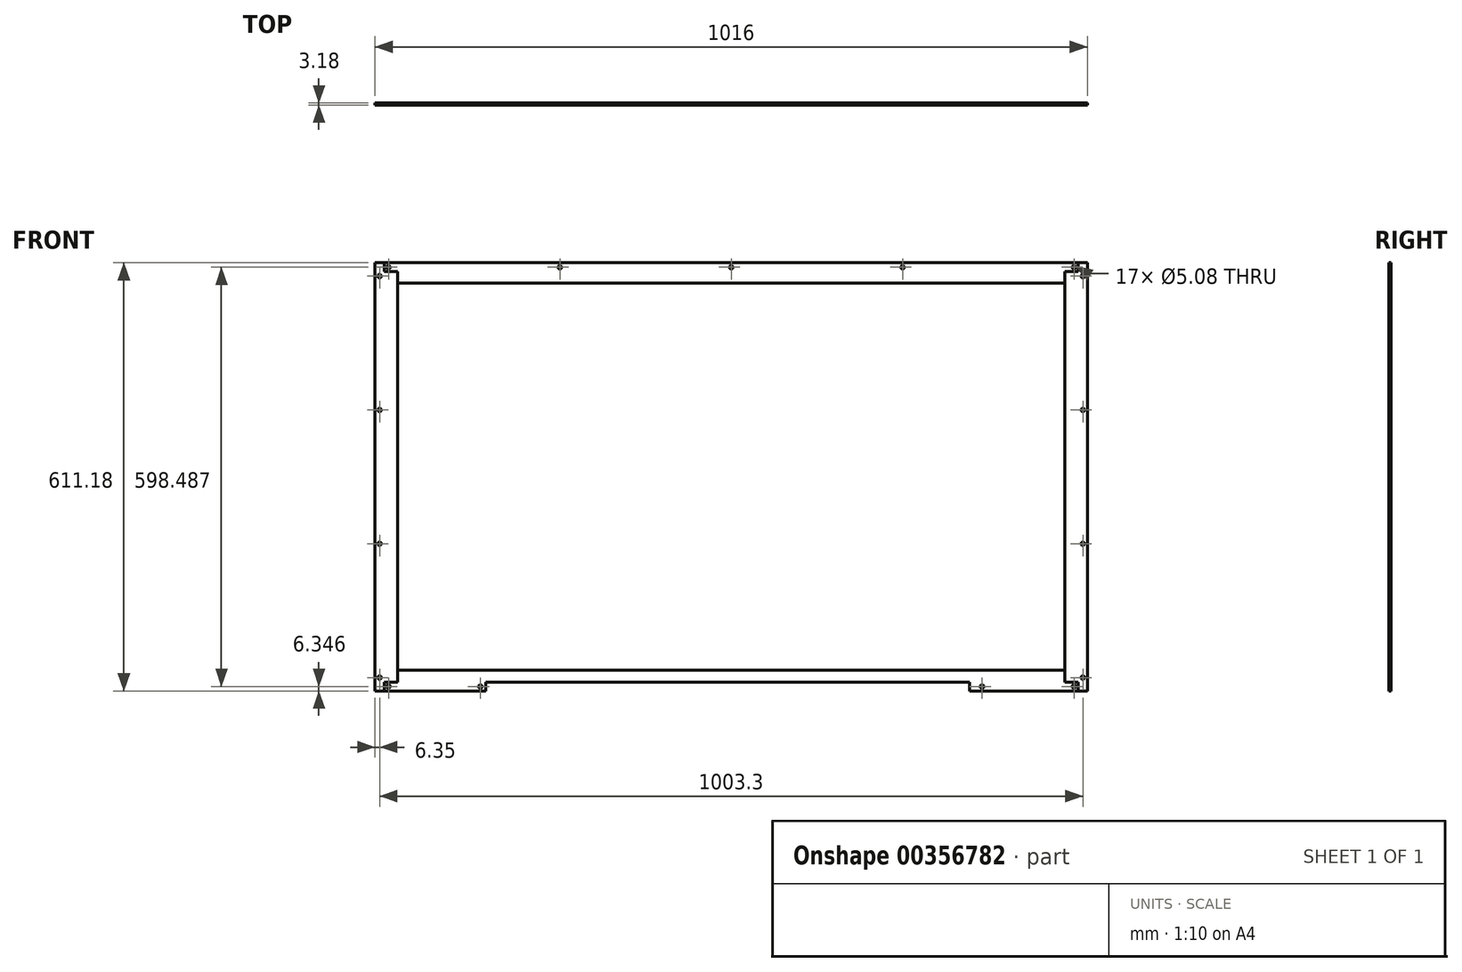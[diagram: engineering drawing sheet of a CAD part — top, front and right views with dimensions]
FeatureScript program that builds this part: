
annotation { "Feature Type Name" : "Feature", "Feature Type Description" : "" }
export const myFeature = defineFeature(function(context is Context, id is Id, definition is map)
    precondition{}
    {
        {
            var Q0;
            Q0=qCreatedBy(makeId("Front.planeOp"),FACE);
            var sketch = newSketch(context, id + "F0", { "sketchPlane" : qUnion([Q0])});
            skLineSegment(sketch, "E0.bottom", {"start": v(495.3, 292.9) * mm, "end": v(-495.3, 292.9) * mm});
            skLineSegment(sketch, "E0.top", {"start": v(495.3, -292.9) * mm, "end": v(-495.3, -292.9) * mm});
            skLineSegment(sketch, "E0.left", {"start": v(495.3, 292.9) * mm, "end": v(495.3, -292.9) * mm});
            skLineSegment(sketch, "E0.right", {"start": v(-495.3, 292.9) * mm, "end": v(-495.3, -292.9) * mm});
            skPoint(sketch, "E0.middle", {"position": v(0, 0) * mm});
            skLineSegment(sketch, "E1.0", {"start": v(-508, 305.6) * mm, "end": v(-508, -305.6) * mm});
            skLineSegment(sketch, "E1.1", {"start": v(508, 305.6) * mm, "end": v(-508, 305.6) * mm});
            skLineSegment(sketch, "E1.2", {"start": v(508, 305.6) * mm, "end": v(508, -305.6) * mm});
            skLineSegment(sketch, "E1.3", {"start": v(508, -305.6) * mm, "end": v(-508, -305.6) * mm});
            skLineSegment(sketch, "E2", {"start": v(-508, 305.6) * mm, "end": v(-495.3, 292.9) * mm});
            skPoint(sketch, "E3.middle", {"position": v(-501.65, 299.24) * mm});
            skLineSegment(sketch, "E4.bottom", {"start": v(-355.3, -296.7) * mm, "end": v(-360.38, -296.7) * mm});
            skLineSegment(sketch, "E4.top", {"start": v(-355.3, -301.78) * mm, "end": v(-360.38, -301.78) * mm});
            skLineSegment(sketch, "E4.left", {"start": v(-355.3, -296.7) * mm, "end": v(-355.3, -301.78) * mm});
            skLineSegment(sketch, "E4.right", {"start": v(-360.38, -296.7) * mm, "end": v(-360.38, -301.78) * mm});
            skPoint(sketch, "E4.middle", {"position": v(-357.84, -299.24) * mm});
            skLineSegment(sketch, "E5.MirrorCS", {"start": v(360.38, -296.7) * mm, "end": v(360.38, -301.78) * mm});
            skLineSegment(sketch, "E6.MirrorCS", {"start": v(355.3, -296.7) * mm, "end": v(360.38, -296.7) * mm});
            skLineSegment(sketch, "E7.MirrorCS", {"start": v(355.3, -296.7) * mm, "end": v(355.3, -301.78) * mm});
            skLineSegment(sketch, "E8.MirrorCS", {"start": v(355.3, -301.78) * mm, "end": v(360.38, -301.78) * mm});
            skLineSegment(sketch, "E9.bottom", {"start": v(-486.41, 296.7) * mm, "end": v(-491.5, 296.7) * mm});
            skLineSegment(sketch, "E9.top", {"start": v(-486.41, 301.78) * mm, "end": v(-491.5, 301.78) * mm});
            skLineSegment(sketch, "E9.left", {"start": v(-486.41, 296.7) * mm, "end": v(-486.41, 301.78) * mm});
            skLineSegment(sketch, "E9.right", {"start": v(-491.5, 296.7) * mm, "end": v(-491.5, 301.78) * mm});
            skPoint(sketch, "E9.middle", {"position": v(-488.95, 299.24) * mm});
            skLineSegment(sketch, "E10.MirrorCS", {"start": v(-504.2, 284) * mm, "end": v(-504.2, 289.08) * mm});
            skLineSegment(sketch, "E11.MirrorCS", {"start": v(-499.11, 289.08) * mm, "end": v(-504.2, 289.08) * mm});
            skLineSegment(sketch, "E12.MirrorCS", {"start": v(-499.11, 284) * mm, "end": v(-499.11, 289.08) * mm});
            skLineSegment(sketch, "E13.MirrorCS", {"start": v(-499.11, 284) * mm, "end": v(-504.2, 284) * mm});
            skCircle(sketch, "E14", {"center": v(-488.95, 299.24) * mm, "radius": 5.97 * mm});
            skLineSegment(sketch, "E15.MirrorCS", {"start": v(499.11, 284) * mm, "end": v(499.11, 289.08) * mm});
            skLineSegment(sketch, "E16.MirrorCS", {"start": v(499.11, 284) * mm, "end": v(504.2, 284) * mm});
            skLineSegment(sketch, "E17.MirrorCS", {"start": v(499.11, 289.08) * mm, "end": v(504.2, 289.08) * mm});
            skLineSegment(sketch, "E18.MirrorCS", {"start": v(504.2, 284) * mm, "end": v(504.2, 289.08) * mm});
            skLineSegment(sketch, "E19.MirrorCS", {"start": v(486.41, 301.78) * mm, "end": v(491.5, 301.78) * mm});
            skLineSegment(sketch, "E20.MirrorCS", {"start": v(486.41, 296.7) * mm, "end": v(486.41, 301.78) * mm});
            skLineSegment(sketch, "E21.MirrorCS", {"start": v(486.41, 296.7) * mm, "end": v(491.5, 296.7) * mm});
            skLineSegment(sketch, "E22.MirrorCS", {"start": v(491.5, 296.7) * mm, "end": v(491.5, 301.78) * mm});
            skPoint(sketch, "E23.MirrorP", {"position": v(488.95, 299.24) * mm});
            skLineSegment(sketch, "E24.MirrorCS", {"start": v(-499.11, -289.08) * mm, "end": v(-504.2, -289.08) * mm});
            skLineSegment(sketch, "E25.MirrorCS", {"start": v(-499.11, -284) * mm, "end": v(-499.11, -289.08) * mm});
            skLineSegment(sketch, "E26.MirrorCS", {"start": v(-499.11, -284) * mm, "end": v(-504.2, -284) * mm});
            skLineSegment(sketch, "E27.MirrorCS", {"start": v(-504.2, -284) * mm, "end": v(-504.2, -289.08) * mm});
            skLineSegment(sketch, "E28.MirrorCS", {"start": v(-486.41, -301.78) * mm, "end": v(-491.5, -301.78) * mm});
            skLineSegment(sketch, "E29.MirrorCS", {"start": v(-491.5, -296.7) * mm, "end": v(-491.5, -301.78) * mm});
            skPoint(sketch, "E30.MirrorP", {"position": v(-488.95, -299.24) * mm});
            skLineSegment(sketch, "E31.MirrorCS", {"start": v(-486.41, -296.7) * mm, "end": v(-486.41, -301.78) * mm});
            skLineSegment(sketch, "E32.MirrorCS", {"start": v(-486.41, -296.7) * mm, "end": v(-491.5, -296.7) * mm});
            skLineSegment(sketch, "E33.MirrorCS", {"start": v(486.41, -296.7) * mm, "end": v(486.41, -301.78) * mm});
            skPoint(sketch, "E34.MirrorP", {"position": v(488.95, -299.24) * mm});
            skLineSegment(sketch, "E35.MirrorCS", {"start": v(491.5, -296.7) * mm, "end": v(491.5, -301.78) * mm});
            skLineSegment(sketch, "E36.MirrorCS", {"start": v(486.41, -296.7) * mm, "end": v(491.5, -296.7) * mm});
            skLineSegment(sketch, "E37.MirrorCS", {"start": v(486.41, -301.78) * mm, "end": v(491.5, -301.78) * mm});
            skLineSegment(sketch, "E38.MirrorCS", {"start": v(499.11, -289.08) * mm, "end": v(504.2, -289.08) * mm});
            skLineSegment(sketch, "E39.MirrorCS", {"start": v(504.2, -284) * mm, "end": v(504.2, -289.08) * mm});
            skLineSegment(sketch, "E40.MirrorCS", {"start": v(499.11, -284) * mm, "end": v(499.11, -289.08) * mm});
            skLineSegment(sketch, "E41.MirrorCS", {"start": v(499.11, -284) * mm, "end": v(504.2, -284) * mm});
            skLineSegment(sketch, "E42.bottom", {"start": v(-504.19, 92.97) * mm, "end": v(-499.11, 92.97) * mm});
            skLineSegment(sketch, "E42.top", {"start": v(-504.19, 98.05) * mm, "end": v(-499.11, 98.05) * mm});
            skLineSegment(sketch, "E42.left", {"start": v(-504.2, 92.97) * mm, "end": v(-504.2, 98.05) * mm});
            skLineSegment(sketch, "E42.right", {"start": v(-499.11, 92.97) * mm, "end": v(-499.11, 98.05) * mm});
            skPoint(sketch, "E42.middle", {"position": v(-501.65, 95.51) * mm});
            skLineSegment(sketch, "E43.bottom", {"start": v(-499.11, -92.97) * mm, "end": v(-504.19, -92.97) * mm});
            skLineSegment(sketch, "E43.top", {"start": v(-499.11, -98.05) * mm, "end": v(-504.19, -98.05) * mm});
            skLineSegment(sketch, "E43.left", {"start": v(-499.11, -92.97) * mm, "end": v(-499.11, -98.05) * mm});
            skLineSegment(sketch, "E43.right", {"start": v(-504.2, -92.97) * mm, "end": v(-504.2, -98.05) * mm});
            skPoint(sketch, "E43.middle", {"position": v(-501.65, -95.51) * mm});
            skLineSegment(sketch, "E44", {"start": v(-501.65, -284) * mm, "end": v(-501.65, -98.05) * mm});
            skLineSegment(sketch, "E45", {"start": v(-501.65, -92.97) * mm, "end": v(-501.65, 92.97) * mm});
            skLineSegment(sketch, "E46", {"start": v(-501.65, 98.05) * mm, "end": v(-501.65, 284) * mm});
            skLineSegment(sketch, "E47.bottom", {"start": v(2.54, 301.78) * mm, "end": v(-2.54, 301.78) * mm});
            skLineSegment(sketch, "E47.top", {"start": v(2.54, 296.7) * mm, "end": v(-2.54, 296.7) * mm});
            skLineSegment(sketch, "E47.left", {"start": v(2.54, 301.78) * mm, "end": v(2.54, 296.7) * mm});
            skLineSegment(sketch, "E47.right", {"start": v(-2.54, 301.78) * mm, "end": v(-2.54, 296.7) * mm});
            skPoint(sketch, "E47.middle", {"position": v(0, 299.24) * mm});
            skPoint(sketch, "E47.middle.positionSnap0", {"position": v(0, 305.6) * mm});
            skPoint(sketch, "E47.centerSnap0", {"position": v(0, 305.6) * mm});
            skLineSegment(sketch, "E48.bottom", {"start": v(-241.94, 301.78) * mm, "end": v(-247.02, 301.78) * mm});
            skLineSegment(sketch, "E48.top", {"start": v(-241.94, 296.7) * mm, "end": v(-247.02, 296.7) * mm});
            skLineSegment(sketch, "E48.left", {"start": v(-241.94, 301.78) * mm, "end": v(-241.94, 296.7) * mm});
            skLineSegment(sketch, "E48.right", {"start": v(-247.02, 301.78) * mm, "end": v(-247.02, 296.7) * mm});
            skPoint(sketch, "E48.middle", {"position": v(-244.48, 299.24) * mm});
            skLineSegment(sketch, "E49.MirrorCS", {"start": v(241.94, 296.7) * mm, "end": v(247.02, 296.7) * mm});
            skPoint(sketch, "E50.MirrorP", {"position": v(244.48, 299.24) * mm});
            skLineSegment(sketch, "E51.MirrorCS", {"start": v(247.02, 301.78) * mm, "end": v(247.02, 296.7) * mm});
            skLineSegment(sketch, "E52.MirrorCS", {"start": v(241.94, 301.78) * mm, "end": v(247.02, 301.78) * mm});
            skLineSegment(sketch, "E53.MirrorCS", {"start": v(241.94, 301.78) * mm, "end": v(241.94, 296.7) * mm});
            skLineSegment(sketch, "E54.MirrorCS", {"start": v(504.19, 92.97) * mm, "end": v(499.11, 92.97) * mm});
            skLineSegment(sketch, "E55.MirrorCS", {"start": v(499.11, 92.97) * mm, "end": v(499.11, 98.05) * mm});
            skPoint(sketch, "E56.MirrorP", {"position": v(501.65, 95.51) * mm});
            skLineSegment(sketch, "E57.MirrorCS", {"start": v(504.19, 98.05) * mm, "end": v(499.11, 98.05) * mm});
            skLineSegment(sketch, "E58.MirrorCS", {"start": v(504.2, 92.97) * mm, "end": v(504.2, 98.05) * mm});
            skLineSegment(sketch, "E59.MirrorCS", {"start": v(499.11, -98.05) * mm, "end": v(504.19, -98.05) * mm});
            skLineSegment(sketch, "E60.MirrorCS", {"start": v(499.11, -92.97) * mm, "end": v(499.11, -98.05) * mm});
            skLineSegment(sketch, "E61.MirrorCS", {"start": v(499.11, -92.97) * mm, "end": v(504.19, -92.97) * mm});
            skPoint(sketch, "E62.MirrorP", {"position": v(501.65, -95.51) * mm});
            skLineSegment(sketch, "E63.MirrorCS", {"start": v(504.2, -92.97) * mm, "end": v(504.2, -98.05) * mm});
            skCircle(sketch, "E64", {"center": v(-488.95, 299.24) * mm, "radius": 2.54 * mm});
            skCircle(sketch, "E65", {"center": v(-501.65, 286.54) * mm, "radius": 2.54 * mm});
            skPoint(sketch, "E65.centerSnap0", {"position": v(-499.11, 286.54) * mm});
            skPoint(sketch, "E65.centerSnap1", {"position": v(-501.65, 289.08) * mm});
            skCircle(sketch, "E66", {"center": v(-501.65, 95.51) * mm, "radius": 2.54 * mm});
            skCircle(sketch, "E67", {"center": v(-501.65, -95.51) * mm, "radius": 2.54 * mm});
            skCircle(sketch, "E68", {"center": v(-501.65, -286.54) * mm, "radius": 2.54 * mm});
            skPoint(sketch, "E68.centerSnap0", {"position": v(-499.11, -286.54) * mm});
            skPoint(sketch, "E68.centerSnap1", {"position": v(-501.65, -289.08) * mm});
            skCircle(sketch, "E69", {"center": v(-488.95, -299.24) * mm, "radius": 2.54 * mm});
            skCircle(sketch, "E70", {"center": v(-357.84, -299.24) * mm, "radius": 2.54 * mm});
            skCircle(sketch, "E71", {"center": v(357.84, -299.24) * mm, "radius": 2.54 * mm});
            skPoint(sketch, "E71.centerSnap0", {"position": v(357.84, -296.7) * mm});
            skCircle(sketch, "E72", {"center": v(488.95, -299.24) * mm, "radius": 2.54 * mm});
            skCircle(sketch, "E73", {"center": v(501.65, -286.54) * mm, "radius": 2.54 * mm});
            skPoint(sketch, "E73.centerSnap0", {"position": v(501.65, -289.08) * mm});
            skPoint(sketch, "E73.centerSnap1", {"position": v(499.11, -286.54) * mm});
            skCircle(sketch, "E74", {"center": v(501.65, -95.51) * mm, "radius": 2.54 * mm});
            skCircle(sketch, "E75", {"center": v(501.65, 95.51) * mm, "radius": 2.54 * mm});
            skCircle(sketch, "E76", {"center": v(501.65, 286.54) * mm, "radius": 2.54 * mm});
            skPoint(sketch, "E76.centerSnap0", {"position": v(504.19, 286.54) * mm});
            skPoint(sketch, "E76.centerSnap1", {"position": v(501.65, 289.08) * mm});
            skCircle(sketch, "E77", {"center": v(488.95, 299.24) * mm, "radius": 2.54 * mm});
            skCircle(sketch, "E78", {"center": v(244.48, 299.24) * mm, "radius": 2.54 * mm});
            skCircle(sketch, "E79", {"center": v(0, 299.24) * mm, "radius": 2.54 * mm});
            skCircle(sketch, "E80", {"center": v(-244.48, 299.24) * mm, "radius": 2.54 * mm});
            skLineSegment(sketch, "E81", {"start": v(-495.3, 292.9) * mm, "end": v(-508, 292.9) * mm});
            skLineSegment(sketch, "E82", {"start": v(495.3, 292.9) * mm, "end": v(508, 292.9) * mm});
            skLineSegment(sketch, "E83", {"start": v(-495.3, -292.9) * mm, "end": v(-508, -292.9) * mm});
            skLineSegment(sketch, "E84", {"start": v(495.3, -292.9) * mm, "end": v(508, -292.9) * mm});
            skLineSegment(sketch, "E85", {"start": v(-350.3, -292.9) * mm, "end": v(-350.3, -305.6) * mm});
            skLineSegment(sketch, "E86", {"start": v(340.3, -292.9) * mm, "end": v(340.3, -305.6) * mm});
            skLineSegment(sketch, "E87.bottom", {"start": v(476, 276.23) * mm, "end": v(-476, 276.23) * mm});
            skLineSegment(sketch, "E87.top", {"start": v(476, -276.22) * mm, "end": v(-476, -276.23) * mm});
            skLineSegment(sketch, "E87.left", {"start": v(476, 276.23) * mm, "end": v(476, -276.23) * mm});
            skLineSegment(sketch, "E87.right", {"start": v(-476, 276.23) * mm, "end": v(-476, -276.23) * mm});
            skLineSegment(sketch, "E88", {"start": v(-476, 276.23) * mm, "end": v(-476, 292.9) * mm});
            skLineSegment(sketch, "E89", {"start": v(-495.3, 292.9) * mm, "end": v(-495.3, 305.6) * mm});
            skLineSegment(sketch, "E90", {"start": v(-476, -276.23) * mm, "end": v(-476, -292.9) * mm});
            skLineSegment(sketch, "E91", {"start": v(-495.3, -292.9) * mm, "end": v(-495.3, -305.6) * mm});
            skLineSegment(sketch, "E92", {"start": v(476, 276.23) * mm, "end": v(476, 292.9) * mm});
            skLineSegment(sketch, "E93", {"start": v(495.3, 292.9) * mm, "end": v(495.3, 305.6) * mm});
            skLineSegment(sketch, "E94", {"start": v(-350.3, -292.9) * mm, "end": v(-350.3, -276.23) * mm});
            skLineSegment(sketch, "E95", {"start": v(476, -276.22) * mm, "end": v(476, -292.9) * mm});
            skLineSegment(sketch, "E96", {"start": v(340.3, -292.9) * mm, "end": v(340.3, -276.22) * mm});
            skLineSegment(sketch, "E97", {"start": v(495.3, -292.9) * mm, "end": v(495.3, -305.6) * mm});
            skSolve(sketch);
        }
        {
            var Q0;
            {var subQ3=sQuery(id+"F0.wireOp",EDGE,"E83");Q0=makeQuery(id+"F0.imprint","IMPRINT",FACE,{"disambiguationData":[TD([[makeQuery(id+"F0.imprint","IMPRINT",EDGE,{"derivedFrom":subQ3}),1.0]])]});}
            var Q1;
            {var subQ0=sQuery(id+"F0.wireOp",EDGE,"E0.right");Q1=makeQuery(id+"F0.imprint","IMPRINT",FACE,{"disambiguationData":[TD([[makeQuery(id+"F0.imprint","IMPRINT",EDGE,{"derivedFrom":subQ0}),1.0]])]});}
            var Q2;
            Q2=makeQuery(id+"F0.imprint","IMPRINT",FACE,{"disambiguationData":[TD([[makeQuery(id+"F0.imprint","IMPRINT",EDGE,{"derivedFrom":sQuery(id+"F0.wireOp",EDGE,"E0.right")}),-1.0]])]});
            var Q3;
            {var subQ0=sQuery(id+"F0.wireOp",EDGE,"E27.MirrorCS");var subQ1=sQuery(id+"F0.wireOp",EDGE,"E26.MirrorCS");var subQ2=makeQuery(id+"F0.imprint","INTERSECT",VERTEX,{"derivedFrom":[subQ1,subQ0]});Q3=makeQuery(id+"F0.imprint","IMPRINT",FACE,{"disambiguationData":[TD([[makeQuery(id+"F0.imprint","IMPRINT",EDGE,{"disambiguationData":[TD([[subQ2,1.0]])],"derivedFrom":subQ1}),1.0]])]});}
            var Q4;
            {var subQ0=sQuery(id+"F0.wireOp",EDGE,"E27.MirrorCS");var subQ1=sQuery(id+"F0.wireOp",EDGE,"E24.MirrorCS");var subQ2=makeQuery(id+"F0.imprint","INTERSECT",VERTEX,{"derivedFrom":[subQ1,subQ0]});Q4=makeQuery(id+"F0.imprint","IMPRINT",FACE,{"disambiguationData":[TD([[makeQuery(id+"F0.imprint","IMPRINT",EDGE,{"disambiguationData":[TD([[subQ2,1.0]])],"derivedFrom":subQ1}),-1.0]])]});}
            var Q5;
            {var subQ0=sQuery(id+"F0.wireOp",EDGE,"E25.MirrorCS");var subQ1=sQuery(id+"F0.wireOp",EDGE,"E24.MirrorCS");var subQ2=makeQuery(id+"F0.imprint","INTERSECT",VERTEX,{"derivedFrom":[subQ1,subQ0]});Q5=makeQuery(id+"F0.imprint","IMPRINT",FACE,{"disambiguationData":[TD([[makeQuery(id+"F0.imprint","IMPRINT",EDGE,{"disambiguationData":[TD([[subQ2,-1.0]])],"derivedFrom":subQ1}),-1.0]])]});}
            var Q6;
            {var subQ0=sQuery(id+"F0.wireOp",EDGE,"E26.MirrorCS");var subQ1=sQuery(id+"F0.wireOp",EDGE,"E25.MirrorCS");var subQ2=makeQuery(id+"F0.imprint","INTERSECT",VERTEX,{"derivedFrom":[subQ1,subQ0]});Q6=makeQuery(id+"F0.imprint","IMPRINT",FACE,{"disambiguationData":[TD([[makeQuery(id+"F0.imprint","IMPRINT",EDGE,{"disambiguationData":[TD([[subQ2,-1.0]])],"derivedFrom":subQ1}),-1.0]])]});}
            var Q7;
            {var subQ0=sQuery(id+"F0.wireOp",EDGE,"E43.right");var subQ1=sQuery(id+"F0.wireOp",EDGE,"E43.bottom");var subQ2=makeQuery(id+"F0.imprint","INTERSECT",VERTEX,{"derivedFrom":[subQ1,subQ0]});Q7=makeQuery(id+"F0.imprint","IMPRINT",FACE,{"disambiguationData":[TD([[makeQuery(id+"F0.imprint","IMPRINT",EDGE,{"disambiguationData":[TD([[subQ2,1.0]])],"derivedFrom":subQ1}),1.0]])]});}
            var Q8;
            {var subQ0=sQuery(id+"F0.wireOp",EDGE,"E43.left");var subQ1=sQuery(id+"F0.wireOp",EDGE,"E43.bottom");var subQ2=makeQuery(id+"F0.imprint","INTERSECT",VERTEX,{"derivedFrom":[subQ1,subQ0]});Q8=makeQuery(id+"F0.imprint","IMPRINT",FACE,{"disambiguationData":[TD([[makeQuery(id+"F0.imprint","IMPRINT",EDGE,{"disambiguationData":[TD([[subQ2,-1.0]])],"derivedFrom":subQ1}),1.0]])]});}
            var Q9;
            {var subQ0=sQuery(id+"F0.wireOp",EDGE,"E43.right");var subQ1=sQuery(id+"F0.wireOp",EDGE,"E43.top");var subQ2=makeQuery(id+"F0.imprint","INTERSECT",VERTEX,{"derivedFrom":[subQ1,subQ0]});Q9=makeQuery(id+"F0.imprint","IMPRINT",FACE,{"disambiguationData":[TD([[makeQuery(id+"F0.imprint","IMPRINT",EDGE,{"disambiguationData":[TD([[subQ2,1.0]])],"derivedFrom":subQ1}),-1.0]])]});}
            var Q10;
            {var subQ0=sQuery(id+"F0.wireOp",EDGE,"E43.left");var subQ1=sQuery(id+"F0.wireOp",EDGE,"E43.top");var subQ2=makeQuery(id+"F0.imprint","INTERSECT",VERTEX,{"derivedFrom":[subQ1,subQ0]});Q10=makeQuery(id+"F0.imprint","IMPRINT",FACE,{"disambiguationData":[TD([[makeQuery(id+"F0.imprint","IMPRINT",EDGE,{"disambiguationData":[TD([[subQ2,-1.0]])],"derivedFrom":subQ1}),-1.0]])]});}
            var Q11;
            {var subQ0=sQuery(id+"F0.wireOp",EDGE,"E42.left");var subQ1=sQuery(id+"F0.wireOp",EDGE,"E42.top");var subQ2=makeQuery(id+"F0.imprint","INTERSECT",VERTEX,{"derivedFrom":[subQ1,subQ0]});Q11=makeQuery(id+"F0.imprint","IMPRINT",FACE,{"disambiguationData":[TD([[makeQuery(id+"F0.imprint","IMPRINT",EDGE,{"disambiguationData":[TD([[subQ2,-1.0]])],"derivedFrom":subQ1}),-1.0]])]});}
            var Q12;
            {var subQ0=sQuery(id+"F0.wireOp",EDGE,"E42.right");var subQ1=sQuery(id+"F0.wireOp",EDGE,"E42.top");var subQ2=makeQuery(id+"F0.imprint","INTERSECT",VERTEX,{"derivedFrom":[subQ1,subQ0]});Q12=makeQuery(id+"F0.imprint","IMPRINT",FACE,{"disambiguationData":[TD([[makeQuery(id+"F0.imprint","IMPRINT",EDGE,{"disambiguationData":[TD([[subQ2,1.0]])],"derivedFrom":subQ1}),-1.0]])]});}
            var Q13;
            {var subQ0=sQuery(id+"F0.wireOp",EDGE,"E42.right");var subQ1=sQuery(id+"F0.wireOp",EDGE,"E42.bottom");var subQ2=makeQuery(id+"F0.imprint","INTERSECT",VERTEX,{"derivedFrom":[subQ1,subQ0]});Q13=makeQuery(id+"F0.imprint","IMPRINT",FACE,{"disambiguationData":[TD([[makeQuery(id+"F0.imprint","IMPRINT",EDGE,{"disambiguationData":[TD([[subQ2,1.0]])],"derivedFrom":subQ1}),1.0]])]});}
            var Q14;
            {var subQ0=sQuery(id+"F0.wireOp",EDGE,"E42.left");var subQ1=sQuery(id+"F0.wireOp",EDGE,"E42.bottom");var subQ2=makeQuery(id+"F0.imprint","INTERSECT",VERTEX,{"derivedFrom":[subQ1,subQ0]});Q14=makeQuery(id+"F0.imprint","IMPRINT",FACE,{"disambiguationData":[TD([[makeQuery(id+"F0.imprint","IMPRINT",EDGE,{"disambiguationData":[TD([[subQ2,-1.0]])],"derivedFrom":subQ1}),1.0]])]});}
            var Q15;
            {var subQ0=sQuery(id+"F0.wireOp",EDGE,"E13.MirrorCS");var subQ1=sQuery(id+"F0.wireOp",EDGE,"E10.MirrorCS");var subQ2=makeQuery(id+"F0.imprint","INTERSECT",VERTEX,{"derivedFrom":[subQ1,subQ0]});Q15=makeQuery(id+"F0.imprint","IMPRINT",FACE,{"disambiguationData":[TD([[makeQuery(id+"F0.imprint","IMPRINT",EDGE,{"disambiguationData":[TD([[subQ2,-1.0]])],"derivedFrom":subQ1}),-1.0]])]});}
            var Q16;
            {var subQ0=sQuery(id+"F0.wireOp",EDGE,"E11.MirrorCS");var subQ1=sQuery(id+"F0.wireOp",EDGE,"E10.MirrorCS");var subQ2=makeQuery(id+"F0.imprint","INTERSECT",VERTEX,{"derivedFrom":[subQ1,subQ0]});Q16=makeQuery(id+"F0.imprint","IMPRINT",FACE,{"disambiguationData":[TD([[makeQuery(id+"F0.imprint","IMPRINT",EDGE,{"disambiguationData":[TD([[subQ2,1.0]])],"derivedFrom":subQ1}),-1.0]])]});}
            var Q17;
            {var subQ0=sQuery(id+"F0.wireOp",EDGE,"E12.MirrorCS");var subQ1=sQuery(id+"F0.wireOp",EDGE,"E11.MirrorCS");var subQ2=makeQuery(id+"F0.imprint","INTERSECT",VERTEX,{"derivedFrom":[subQ1,subQ0]});Q17=makeQuery(id+"F0.imprint","IMPRINT",FACE,{"disambiguationData":[TD([[makeQuery(id+"F0.imprint","IMPRINT",EDGE,{"disambiguationData":[TD([[subQ2,-1.0]])],"derivedFrom":subQ1}),1.0]])]});}
            var Q18;
            {var subQ0=sQuery(id+"F0.wireOp",EDGE,"E13.MirrorCS");var subQ1=sQuery(id+"F0.wireOp",EDGE,"E12.MirrorCS");var subQ2=makeQuery(id+"F0.imprint","INTERSECT",VERTEX,{"derivedFrom":[subQ1,subQ0]});Q18=makeQuery(id+"F0.imprint","IMPRINT",FACE,{"disambiguationData":[TD([[makeQuery(id+"F0.imprint","IMPRINT",EDGE,{"disambiguationData":[TD([[subQ2,-1.0]])],"derivedFrom":subQ1}),1.0]])]});}
            var Q19;
            {var subQ0=sQuery(id+"F0.wireOp",EDGE,"E2");Q19=makeQuery(id+"F0.imprint","IMPRINT",FACE,{"disambiguationData":[TD([[makeQuery(id+"F0.imprint","IMPRINT",EDGE,{"derivedFrom":subQ0}),-1.0]])]});}
            var Q20;
            {var subQ0=sQuery(id+"F0.wireOp",EDGE,"E2");Q20=makeQuery(id+"F0.imprint","IMPRINT",FACE,{"disambiguationData":[TD([[makeQuery(id+"F0.imprint","IMPRINT",EDGE,{"derivedFrom":subQ0}),1.0]])]});}
            extrude(context, id + "F1", {"entities" : qUnion([Q0, Q1, Q2, Q3, Q4, Q5, Q6, Q7, Q8, Q9, Q10, Q11, Q12, Q13, Q14, Q15, Q16, Q17, Q18, Q19, Q20]), "endBound" : BoundingType.SYMMETRIC, "depth" : 3.17 * mm});
        }
        {
            var Q0;
            Q0=makeQuery(id+"F0.imprint","IMPRINT",FACE,{"disambiguationData":[TD([[makeQuery(id+"F0.imprint","IMPRINT",EDGE,{"derivedFrom":sQuery(id+"F0.wireOp",EDGE,"E14")}),-1.0]])]});
            var Q1;
            Q1=makeQuery(id+"F0.imprint","IMPRINT",FACE,{"disambiguationData":[TD([[makeQuery(id+"F0.imprint","IMPRINT",EDGE,{"derivedFrom":sQuery(id+"F0.wireOp",EDGE,"E14")}),1.0]])]});
            var Q2;
            {var subQ0=sQuery(id+"F0.wireOp",EDGE,"E9.left");var subQ1=sQuery(id+"F0.wireOp",EDGE,"E9.bottom");var subQ2=makeQuery(id+"F0.imprint","INTERSECT",VERTEX,{"derivedFrom":[subQ1,subQ0]});Q2=makeQuery(id+"F0.imprint","IMPRINT",FACE,{"disambiguationData":[TD([[makeQuery(id+"F0.imprint","IMPRINT",EDGE,{"disambiguationData":[TD([[subQ2,-1.0]])],"derivedFrom":subQ1}),-1.0]])]});}
            var Q3;
            {var subQ0=sQuery(id+"F0.wireOp",EDGE,"E9.right");var subQ1=sQuery(id+"F0.wireOp",EDGE,"E9.bottom");var subQ2=makeQuery(id+"F0.imprint","INTERSECT",VERTEX,{"derivedFrom":[subQ1,subQ0]});Q3=makeQuery(id+"F0.imprint","IMPRINT",FACE,{"disambiguationData":[TD([[makeQuery(id+"F0.imprint","IMPRINT",EDGE,{"disambiguationData":[TD([[subQ2,1.0]])],"derivedFrom":subQ1}),-1.0]])]});}
            var Q4;
            {var subQ0=sQuery(id+"F0.wireOp",EDGE,"E9.right");var subQ1=sQuery(id+"F0.wireOp",EDGE,"E9.top");var subQ2=makeQuery(id+"F0.imprint","INTERSECT",VERTEX,{"derivedFrom":[subQ1,subQ0]});Q4=makeQuery(id+"F0.imprint","IMPRINT",FACE,{"disambiguationData":[TD([[makeQuery(id+"F0.imprint","IMPRINT",EDGE,{"disambiguationData":[TD([[subQ2,1.0]])],"derivedFrom":subQ1}),1.0]])]});}
            var Q5;
            {var subQ0=sQuery(id+"F0.wireOp",EDGE,"E9.left");var subQ1=sQuery(id+"F0.wireOp",EDGE,"E9.top");var subQ2=makeQuery(id+"F0.imprint","INTERSECT",VERTEX,{"derivedFrom":[subQ1,subQ0]});Q5=makeQuery(id+"F0.imprint","IMPRINT",FACE,{"disambiguationData":[TD([[makeQuery(id+"F0.imprint","IMPRINT",EDGE,{"disambiguationData":[TD([[subQ2,-1.0]])],"derivedFrom":subQ1}),1.0]])]});}
            var Q6;
            Q6=makeQuery(id+"F0.imprint","IMPRINT",FACE,{"disambiguationData":[TD([[makeQuery(id+"F0.imprint","IMPRINT",EDGE,{"derivedFrom":sQuery(id+"F0.wireOp",EDGE,"E87.bottom")}),-1.0]])]});
            var Q7;
            {var subQ0=sQuery(id+"F0.wireOp",EDGE,"E48.left");var subQ1=sQuery(id+"F0.wireOp",EDGE,"E48.bottom");var subQ2=makeQuery(id+"F0.imprint","INTERSECT",VERTEX,{"derivedFrom":[subQ1,subQ0]});Q7=makeQuery(id+"F0.imprint","IMPRINT",FACE,{"disambiguationData":[TD([[makeQuery(id+"F0.imprint","IMPRINT",EDGE,{"disambiguationData":[TD([[subQ2,-1.0]])],"derivedFrom":subQ1}),1.0]])]});}
            var Q8;
            {var subQ0=sQuery(id+"F0.wireOp",EDGE,"E48.right");var subQ1=sQuery(id+"F0.wireOp",EDGE,"E48.bottom");var subQ2=makeQuery(id+"F0.imprint","INTERSECT",VERTEX,{"derivedFrom":[subQ1,subQ0]});Q8=makeQuery(id+"F0.imprint","IMPRINT",FACE,{"disambiguationData":[TD([[makeQuery(id+"F0.imprint","IMPRINT",EDGE,{"disambiguationData":[TD([[subQ2,1.0]])],"derivedFrom":subQ1}),1.0]])]});}
            var Q9;
            {var subQ0=sQuery(id+"F0.wireOp",EDGE,"E48.right");var subQ1=sQuery(id+"F0.wireOp",EDGE,"E48.top");var subQ2=makeQuery(id+"F0.imprint","INTERSECT",VERTEX,{"derivedFrom":[subQ1,subQ0]});Q9=makeQuery(id+"F0.imprint","IMPRINT",FACE,{"disambiguationData":[TD([[makeQuery(id+"F0.imprint","IMPRINT",EDGE,{"disambiguationData":[TD([[subQ2,1.0]])],"derivedFrom":subQ1}),-1.0]])]});}
            var Q10;
            {var subQ0=sQuery(id+"F0.wireOp",EDGE,"E48.left");var subQ1=sQuery(id+"F0.wireOp",EDGE,"E48.top");var subQ2=makeQuery(id+"F0.imprint","INTERSECT",VERTEX,{"derivedFrom":[subQ1,subQ0]});Q10=makeQuery(id+"F0.imprint","IMPRINT",FACE,{"disambiguationData":[TD([[makeQuery(id+"F0.imprint","IMPRINT",EDGE,{"disambiguationData":[TD([[subQ2,-1.0]])],"derivedFrom":subQ1}),-1.0]])]});}
            var Q11;
            {var subQ0=sQuery(id+"F0.wireOp",EDGE,"E47.right");var subQ1=sQuery(id+"F0.wireOp",EDGE,"E47.bottom");var subQ2=makeQuery(id+"F0.imprint","INTERSECT",VERTEX,{"derivedFrom":[subQ1,subQ0]});Q11=makeQuery(id+"F0.imprint","IMPRINT",FACE,{"disambiguationData":[TD([[makeQuery(id+"F0.imprint","IMPRINT",EDGE,{"disambiguationData":[TD([[subQ2,1.0]])],"derivedFrom":subQ1}),1.0]])]});}
            var Q12;
            {var subQ0=sQuery(id+"F0.wireOp",EDGE,"E47.left");var subQ1=sQuery(id+"F0.wireOp",EDGE,"E47.bottom");var subQ2=makeQuery(id+"F0.imprint","INTERSECT",VERTEX,{"derivedFrom":[subQ1,subQ0]});Q12=makeQuery(id+"F0.imprint","IMPRINT",FACE,{"disambiguationData":[TD([[makeQuery(id+"F0.imprint","IMPRINT",EDGE,{"disambiguationData":[TD([[subQ2,-1.0]])],"derivedFrom":subQ1}),1.0]])]});}
            var Q13;
            {var subQ0=sQuery(id+"F0.wireOp",EDGE,"E47.left");var subQ1=sQuery(id+"F0.wireOp",EDGE,"E47.top");var subQ2=makeQuery(id+"F0.imprint","INTERSECT",VERTEX,{"derivedFrom":[subQ1,subQ0]});Q13=makeQuery(id+"F0.imprint","IMPRINT",FACE,{"disambiguationData":[TD([[makeQuery(id+"F0.imprint","IMPRINT",EDGE,{"disambiguationData":[TD([[subQ2,-1.0]])],"derivedFrom":subQ1}),-1.0]])]});}
            var Q14;
            {var subQ0=sQuery(id+"F0.wireOp",EDGE,"E47.right");var subQ1=sQuery(id+"F0.wireOp",EDGE,"E47.top");var subQ2=makeQuery(id+"F0.imprint","INTERSECT",VERTEX,{"derivedFrom":[subQ1,subQ0]});Q14=makeQuery(id+"F0.imprint","IMPRINT",FACE,{"disambiguationData":[TD([[makeQuery(id+"F0.imprint","IMPRINT",EDGE,{"disambiguationData":[TD([[subQ2,1.0]])],"derivedFrom":subQ1}),-1.0]])]});}
            var Q15;
            {var subQ0=sQuery(id+"F0.wireOp",EDGE,"E53.MirrorCS");var subQ1=sQuery(id+"F0.wireOp",EDGE,"E52.MirrorCS");var subQ2=makeQuery(id+"F0.imprint","INTERSECT",VERTEX,{"derivedFrom":[subQ1,subQ0]});Q15=makeQuery(id+"F0.imprint","IMPRINT",FACE,{"disambiguationData":[TD([[makeQuery(id+"F0.imprint","IMPRINT",EDGE,{"disambiguationData":[TD([[subQ2,-1.0]])],"derivedFrom":subQ1}),-1.0]])]});}
            var Q16;
            {var subQ0=sQuery(id+"F0.wireOp",EDGE,"E52.MirrorCS");var subQ1=sQuery(id+"F0.wireOp",EDGE,"E51.MirrorCS");var subQ2=makeQuery(id+"F0.imprint","INTERSECT",VERTEX,{"derivedFrom":[subQ1,subQ0]});Q16=makeQuery(id+"F0.imprint","IMPRINT",FACE,{"disambiguationData":[TD([[makeQuery(id+"F0.imprint","IMPRINT",EDGE,{"disambiguationData":[TD([[subQ2,-1.0]])],"derivedFrom":subQ1}),-1.0]])]});}
            var Q17;
            {var subQ0=sQuery(id+"F0.wireOp",EDGE,"E53.MirrorCS");var subQ1=sQuery(id+"F0.wireOp",EDGE,"E49.MirrorCS");var subQ2=makeQuery(id+"F0.imprint","INTERSECT",VERTEX,{"derivedFrom":[subQ1,subQ0]});Q17=makeQuery(id+"F0.imprint","IMPRINT",FACE,{"disambiguationData":[TD([[makeQuery(id+"F0.imprint","IMPRINT",EDGE,{"disambiguationData":[TD([[subQ2,-1.0]])],"derivedFrom":subQ1}),1.0]])]});}
            var Q18;
            {var subQ0=sQuery(id+"F0.wireOp",EDGE,"E51.MirrorCS");var subQ1=sQuery(id+"F0.wireOp",EDGE,"E49.MirrorCS");var subQ2=makeQuery(id+"F0.imprint","INTERSECT",VERTEX,{"derivedFrom":[subQ1,subQ0]});Q18=makeQuery(id+"F0.imprint","IMPRINT",FACE,{"disambiguationData":[TD([[makeQuery(id+"F0.imprint","IMPRINT",EDGE,{"disambiguationData":[TD([[subQ2,1.0]])],"derivedFrom":subQ1}),1.0]])]});}
            var Q19;
            {var subQ0=sQuery(id+"F0.wireOp",EDGE,"E20.MirrorCS");var subQ1=sQuery(id+"F0.wireOp",EDGE,"E19.MirrorCS");var subQ2=makeQuery(id+"F0.imprint","INTERSECT",VERTEX,{"derivedFrom":[subQ1,subQ0]});Q19=makeQuery(id+"F0.imprint","IMPRINT",FACE,{"disambiguationData":[TD([[makeQuery(id+"F0.imprint","IMPRINT",EDGE,{"disambiguationData":[TD([[subQ2,-1.0]])],"derivedFrom":subQ1}),-1.0]])]});}
            var Q20;
            {var subQ0=sQuery(id+"F0.wireOp",EDGE,"E22.MirrorCS");var subQ1=sQuery(id+"F0.wireOp",EDGE,"E19.MirrorCS");var subQ2=makeQuery(id+"F0.imprint","INTERSECT",VERTEX,{"derivedFrom":[subQ1,subQ0]});Q20=makeQuery(id+"F0.imprint","IMPRINT",FACE,{"disambiguationData":[TD([[makeQuery(id+"F0.imprint","IMPRINT",EDGE,{"disambiguationData":[TD([[subQ2,1.0]])],"derivedFrom":subQ1}),-1.0]])]});}
            var Q21;
            {var subQ0=sQuery(id+"F0.wireOp",EDGE,"E22.MirrorCS");var subQ1=sQuery(id+"F0.wireOp",EDGE,"E21.MirrorCS");var subQ2=makeQuery(id+"F0.imprint","INTERSECT",VERTEX,{"derivedFrom":[subQ1,subQ0]});Q21=makeQuery(id+"F0.imprint","IMPRINT",FACE,{"disambiguationData":[TD([[makeQuery(id+"F0.imprint","IMPRINT",EDGE,{"disambiguationData":[TD([[subQ2,1.0]])],"derivedFrom":subQ1}),1.0]])]});}
            var Q22;
            {var subQ0=sQuery(id+"F0.wireOp",EDGE,"E21.MirrorCS");var subQ1=sQuery(id+"F0.wireOp",EDGE,"E20.MirrorCS");var subQ2=makeQuery(id+"F0.imprint","INTERSECT",VERTEX,{"derivedFrom":[subQ1,subQ0]});Q22=makeQuery(id+"F0.imprint","IMPRINT",FACE,{"disambiguationData":[TD([[makeQuery(id+"F0.imprint","IMPRINT",EDGE,{"disambiguationData":[TD([[subQ2,-1.0]])],"derivedFrom":subQ1}),-1.0]])]});}
            extrude(context, id + "F2", {"entities" : qUnion([Q0, Q1, Q2, Q3, Q4, Q5, Q6, Q7, Q8, Q9, Q10, Q11, Q12, Q13, Q14, Q15, Q16, Q17, Q18, Q19, Q20, Q21, Q22]), "endBound" : BoundingType.SYMMETRIC, "depth" : 3.17 * mm});
        }
        {
            var Q0;
            {var subQ3=sQuery(id+"F0.wireOp",EDGE,"E84");Q0=makeQuery(id+"F0.imprint","IMPRINT",FACE,{"disambiguationData":[TD([[makeQuery(id+"F0.imprint","IMPRINT",EDGE,{"derivedFrom":subQ3}),-1.0]])]});}
            var Q1;
            {var subQ0=sQuery(id+"F0.wireOp",EDGE,"E0.left");Q1=makeQuery(id+"F0.imprint","IMPRINT",FACE,{"disambiguationData":[TD([[makeQuery(id+"F0.imprint","IMPRINT",EDGE,{"derivedFrom":subQ0}),-1.0]])]});}
            var Q2;
            Q2=makeQuery(id+"F0.imprint","IMPRINT",FACE,{"disambiguationData":[TD([[makeQuery(id+"F0.imprint","IMPRINT",EDGE,{"derivedFrom":sQuery(id+"F0.wireOp",EDGE,"E0.left")}),1.0]])]});
            var Q3;
            {var subQ0=sQuery(id+"F0.wireOp",EDGE,"E40.MirrorCS");var subQ1=sQuery(id+"F0.wireOp",EDGE,"E38.MirrorCS");var subQ2=makeQuery(id+"F0.imprint","INTERSECT",VERTEX,{"derivedFrom":[subQ1,subQ0]});Q3=makeQuery(id+"F0.imprint","IMPRINT",FACE,{"disambiguationData":[TD([[makeQuery(id+"F0.imprint","IMPRINT",EDGE,{"disambiguationData":[TD([[subQ2,-1.0]])],"derivedFrom":subQ1}),1.0]])]});}
            var Q4;
            {var subQ0=sQuery(id+"F0.wireOp",EDGE,"E41.MirrorCS");var subQ1=sQuery(id+"F0.wireOp",EDGE,"E40.MirrorCS");var subQ2=makeQuery(id+"F0.imprint","INTERSECT",VERTEX,{"derivedFrom":[subQ1,subQ0]});Q4=makeQuery(id+"F0.imprint","IMPRINT",FACE,{"disambiguationData":[TD([[makeQuery(id+"F0.imprint","IMPRINT",EDGE,{"disambiguationData":[TD([[subQ2,-1.0]])],"derivedFrom":subQ1}),1.0]])]});}
            var Q5;
            {var subQ0=sQuery(id+"F0.wireOp",EDGE,"E41.MirrorCS");var subQ1=sQuery(id+"F0.wireOp",EDGE,"E39.MirrorCS");var subQ2=makeQuery(id+"F0.imprint","INTERSECT",VERTEX,{"derivedFrom":[subQ1,subQ0]});Q5=makeQuery(id+"F0.imprint","IMPRINT",FACE,{"disambiguationData":[TD([[makeQuery(id+"F0.imprint","IMPRINT",EDGE,{"disambiguationData":[TD([[subQ2,-1.0]])],"derivedFrom":subQ1}),-1.0]])]});}
            var Q6;
            {var subQ0=sQuery(id+"F0.wireOp",EDGE,"E39.MirrorCS");var subQ1=sQuery(id+"F0.wireOp",EDGE,"E38.MirrorCS");var subQ2=makeQuery(id+"F0.imprint","INTERSECT",VERTEX,{"derivedFrom":[subQ1,subQ0]});Q6=makeQuery(id+"F0.imprint","IMPRINT",FACE,{"disambiguationData":[TD([[makeQuery(id+"F0.imprint","IMPRINT",EDGE,{"disambiguationData":[TD([[subQ2,1.0]])],"derivedFrom":subQ1}),1.0]])]});}
            var Q7;
            {var subQ0=sQuery(id+"F0.wireOp",EDGE,"E61.MirrorCS");var subQ1=sQuery(id+"F0.wireOp",EDGE,"E60.MirrorCS");var subQ2=makeQuery(id+"F0.imprint","INTERSECT",VERTEX,{"derivedFrom":[subQ1,subQ0]});Q7=makeQuery(id+"F0.imprint","IMPRINT",FACE,{"disambiguationData":[TD([[makeQuery(id+"F0.imprint","IMPRINT",EDGE,{"disambiguationData":[TD([[subQ2,-1.0]])],"derivedFrom":subQ1}),1.0]])]});}
            var Q8;
            {var subQ0=sQuery(id+"F0.wireOp",EDGE,"E63.MirrorCS");var subQ1=sQuery(id+"F0.wireOp",EDGE,"E61.MirrorCS");var subQ2=makeQuery(id+"F0.imprint","INTERSECT",VERTEX,{"derivedFrom":[subQ1,subQ0]});Q8=makeQuery(id+"F0.imprint","IMPRINT",FACE,{"disambiguationData":[TD([[makeQuery(id+"F0.imprint","IMPRINT",EDGE,{"disambiguationData":[TD([[subQ2,1.0]])],"derivedFrom":subQ1}),-1.0]])]});}
            var Q9;
            {var subQ0=sQuery(id+"F0.wireOp",EDGE,"E63.MirrorCS");var subQ1=sQuery(id+"F0.wireOp",EDGE,"E59.MirrorCS");var subQ2=makeQuery(id+"F0.imprint","INTERSECT",VERTEX,{"derivedFrom":[subQ1,subQ0]});Q9=makeQuery(id+"F0.imprint","IMPRINT",FACE,{"disambiguationData":[TD([[makeQuery(id+"F0.imprint","IMPRINT",EDGE,{"disambiguationData":[TD([[subQ2,1.0]])],"derivedFrom":subQ1}),1.0]])]});}
            var Q10;
            {var subQ0=sQuery(id+"F0.wireOp",EDGE,"E60.MirrorCS");var subQ1=sQuery(id+"F0.wireOp",EDGE,"E59.MirrorCS");var subQ2=makeQuery(id+"F0.imprint","INTERSECT",VERTEX,{"derivedFrom":[subQ1,subQ0]});Q10=makeQuery(id+"F0.imprint","IMPRINT",FACE,{"disambiguationData":[TD([[makeQuery(id+"F0.imprint","IMPRINT",EDGE,{"disambiguationData":[TD([[subQ2,-1.0]])],"derivedFrom":subQ1}),1.0]])]});}
            var Q11;
            {var subQ0=sQuery(id+"F0.wireOp",EDGE,"E57.MirrorCS");var subQ1=sQuery(id+"F0.wireOp",EDGE,"E55.MirrorCS");var subQ2=makeQuery(id+"F0.imprint","INTERSECT",VERTEX,{"derivedFrom":[subQ1,subQ0]});Q11=makeQuery(id+"F0.imprint","IMPRINT",FACE,{"disambiguationData":[TD([[makeQuery(id+"F0.imprint","IMPRINT",EDGE,{"disambiguationData":[TD([[subQ2,1.0]])],"derivedFrom":subQ1}),-1.0]])]});}
            var Q12;
            {var subQ0=sQuery(id+"F0.wireOp",EDGE,"E58.MirrorCS");var subQ1=sQuery(id+"F0.wireOp",EDGE,"E57.MirrorCS");var subQ2=makeQuery(id+"F0.imprint","INTERSECT",VERTEX,{"derivedFrom":[subQ1,subQ0]});Q12=makeQuery(id+"F0.imprint","IMPRINT",FACE,{"disambiguationData":[TD([[makeQuery(id+"F0.imprint","IMPRINT",EDGE,{"disambiguationData":[TD([[subQ2,-1.0]])],"derivedFrom":subQ1}),1.0]])]});}
            var Q13;
            {var subQ0=sQuery(id+"F0.wireOp",EDGE,"E58.MirrorCS");var subQ1=sQuery(id+"F0.wireOp",EDGE,"E54.MirrorCS");var subQ2=makeQuery(id+"F0.imprint","INTERSECT",VERTEX,{"derivedFrom":[subQ1,subQ0]});Q13=makeQuery(id+"F0.imprint","IMPRINT",FACE,{"disambiguationData":[TD([[makeQuery(id+"F0.imprint","IMPRINT",EDGE,{"disambiguationData":[TD([[subQ2,-1.0]])],"derivedFrom":subQ1}),-1.0]])]});}
            var Q14;
            {var subQ0=sQuery(id+"F0.wireOp",EDGE,"E55.MirrorCS");var subQ1=sQuery(id+"F0.wireOp",EDGE,"E54.MirrorCS");var subQ2=makeQuery(id+"F0.imprint","INTERSECT",VERTEX,{"derivedFrom":[subQ1,subQ0]});Q14=makeQuery(id+"F0.imprint","IMPRINT",FACE,{"disambiguationData":[TD([[makeQuery(id+"F0.imprint","IMPRINT",EDGE,{"disambiguationData":[TD([[subQ2,1.0]])],"derivedFrom":subQ1}),-1.0]])]});}
            var Q15;
            {var subQ4=sQuery(id+"F0.wireOp",EDGE,"E82");Q15=makeQuery(id+"F0.imprint","IMPRINT",FACE,{"disambiguationData":[TD([[makeQuery(id+"F0.imprint","IMPRINT",EDGE,{"derivedFrom":subQ4}),1.0]])]});}
            var Q16;
            {var subQ0=sQuery(id+"F0.wireOp",EDGE,"E17.MirrorCS");var subQ1=sQuery(id+"F0.wireOp",EDGE,"E15.MirrorCS");var subQ2=makeQuery(id+"F0.imprint","INTERSECT",VERTEX,{"derivedFrom":[subQ1,subQ0]});Q16=makeQuery(id+"F0.imprint","IMPRINT",FACE,{"disambiguationData":[TD([[makeQuery(id+"F0.imprint","IMPRINT",EDGE,{"disambiguationData":[TD([[subQ2,1.0]])],"derivedFrom":subQ1}),-1.0]])]});}
            var Q17;
            {var subQ0=sQuery(id+"F0.wireOp",EDGE,"E18.MirrorCS");var subQ1=sQuery(id+"F0.wireOp",EDGE,"E17.MirrorCS");var subQ2=makeQuery(id+"F0.imprint","INTERSECT",VERTEX,{"derivedFrom":[subQ1,subQ0]});Q17=makeQuery(id+"F0.imprint","IMPRINT",FACE,{"disambiguationData":[TD([[makeQuery(id+"F0.imprint","IMPRINT",EDGE,{"disambiguationData":[TD([[subQ2,1.0]])],"derivedFrom":subQ1}),-1.0]])]});}
            var Q18;
            {var subQ0=sQuery(id+"F0.wireOp",EDGE,"E18.MirrorCS");var subQ1=sQuery(id+"F0.wireOp",EDGE,"E16.MirrorCS");var subQ2=makeQuery(id+"F0.imprint","INTERSECT",VERTEX,{"derivedFrom":[subQ1,subQ0]});Q18=makeQuery(id+"F0.imprint","IMPRINT",FACE,{"disambiguationData":[TD([[makeQuery(id+"F0.imprint","IMPRINT",EDGE,{"disambiguationData":[TD([[subQ2,1.0]])],"derivedFrom":subQ1}),1.0]])]});}
            var Q19;
            {var subQ0=sQuery(id+"F0.wireOp",EDGE,"E16.MirrorCS");var subQ1=sQuery(id+"F0.wireOp",EDGE,"E15.MirrorCS");var subQ2=makeQuery(id+"F0.imprint","INTERSECT",VERTEX,{"derivedFrom":[subQ1,subQ0]});Q19=makeQuery(id+"F0.imprint","IMPRINT",FACE,{"disambiguationData":[TD([[makeQuery(id+"F0.imprint","IMPRINT",EDGE,{"disambiguationData":[TD([[subQ2,-1.0]])],"derivedFrom":subQ1}),-1.0]])]});}
            extrude(context, id + "F3", {"entities" : qUnion([Q0, Q1, Q2, Q3, Q4, Q5, Q6, Q7, Q8, Q9, Q10, Q11, Q12, Q13, Q14, Q15, Q16, Q17, Q18, Q19]), "endBound" : BoundingType.SYMMETRIC, "depth" : 3.17 * mm});
        }
        {
            var Q0;
            {var subQ13=sQuery(id+"F0.wireOp",EDGE,"E85");Q0=makeQuery(id+"F0.imprint","IMPRINT",FACE,{"disambiguationData":[TD([[makeQuery(id+"F0.imprint","IMPRINT",EDGE,{"derivedFrom":subQ13}),-1.0]])]});}
            var Q1;
            {var subQ2=sQuery(id+"F0.wireOp",EDGE,"E90");Q1=makeQuery(id+"F0.imprint","IMPRINT",FACE,{"disambiguationData":[TD([[makeQuery(id+"F0.imprint","IMPRINT",EDGE,{"derivedFrom":subQ2}),1.0]])]});}
            var Q2;
            {var subQ0=sQuery(id+"F0.wireOp",EDGE,"E31.MirrorCS");var subQ1=sQuery(id+"F0.wireOp",EDGE,"E28.MirrorCS");var subQ2=makeQuery(id+"F0.imprint","INTERSECT",VERTEX,{"derivedFrom":[subQ1,subQ0]});Q2=makeQuery(id+"F0.imprint","IMPRINT",FACE,{"disambiguationData":[TD([[makeQuery(id+"F0.imprint","IMPRINT",EDGE,{"disambiguationData":[TD([[subQ2,-1.0]])],"derivedFrom":subQ1}),-1.0]])]});}
            var Q3;
            {var subQ0=sQuery(id+"F0.wireOp",EDGE,"E29.MirrorCS");var subQ1=sQuery(id+"F0.wireOp",EDGE,"E28.MirrorCS");var subQ2=makeQuery(id+"F0.imprint","INTERSECT",VERTEX,{"derivedFrom":[subQ1,subQ0]});Q3=makeQuery(id+"F0.imprint","IMPRINT",FACE,{"disambiguationData":[TD([[makeQuery(id+"F0.imprint","IMPRINT",EDGE,{"disambiguationData":[TD([[subQ2,1.0]])],"derivedFrom":subQ1}),-1.0]])]});}
            var Q4;
            {var subQ0=sQuery(id+"F0.wireOp",EDGE,"E32.MirrorCS");var subQ1=sQuery(id+"F0.wireOp",EDGE,"E29.MirrorCS");var subQ2=makeQuery(id+"F0.imprint","INTERSECT",VERTEX,{"derivedFrom":[subQ1,subQ0]});Q4=makeQuery(id+"F0.imprint","IMPRINT",FACE,{"disambiguationData":[TD([[makeQuery(id+"F0.imprint","IMPRINT",EDGE,{"disambiguationData":[TD([[subQ2,-1.0]])],"derivedFrom":subQ1}),1.0]])]});}
            var Q5;
            {var subQ0=sQuery(id+"F0.wireOp",EDGE,"E32.MirrorCS");var subQ1=sQuery(id+"F0.wireOp",EDGE,"E31.MirrorCS");var subQ2=makeQuery(id+"F0.imprint","INTERSECT",VERTEX,{"derivedFrom":[subQ1,subQ0]});Q5=makeQuery(id+"F0.imprint","IMPRINT",FACE,{"disambiguationData":[TD([[makeQuery(id+"F0.imprint","IMPRINT",EDGE,{"disambiguationData":[TD([[subQ2,-1.0]])],"derivedFrom":subQ1}),-1.0]])]});}
            var Q6;
            {var subQ0=sQuery(id+"F0.wireOp",EDGE,"E4.right");var subQ1=sQuery(id+"F0.wireOp",EDGE,"E4.bottom");var subQ2=makeQuery(id+"F0.imprint","INTERSECT",VERTEX,{"derivedFrom":[subQ1,subQ0]});Q6=makeQuery(id+"F0.imprint","IMPRINT",FACE,{"disambiguationData":[TD([[makeQuery(id+"F0.imprint","IMPRINT",EDGE,{"disambiguationData":[TD([[subQ2,1.0]])],"derivedFrom":subQ1}),1.0]])]});}
            var Q7;
            {var subQ0=sQuery(id+"F0.wireOp",EDGE,"E4.left");var subQ1=sQuery(id+"F0.wireOp",EDGE,"E4.bottom");var subQ2=makeQuery(id+"F0.imprint","INTERSECT",VERTEX,{"derivedFrom":[subQ1,subQ0]});Q7=makeQuery(id+"F0.imprint","IMPRINT",FACE,{"disambiguationData":[TD([[makeQuery(id+"F0.imprint","IMPRINT",EDGE,{"disambiguationData":[TD([[subQ2,-1.0]])],"derivedFrom":subQ1}),1.0]])]});}
            var Q8;
            {var subQ0=sQuery(id+"F0.wireOp",EDGE,"E4.left");var subQ1=sQuery(id+"F0.wireOp",EDGE,"E4.top");var subQ2=makeQuery(id+"F0.imprint","INTERSECT",VERTEX,{"derivedFrom":[subQ1,subQ0]});Q8=makeQuery(id+"F0.imprint","IMPRINT",FACE,{"disambiguationData":[TD([[makeQuery(id+"F0.imprint","IMPRINT",EDGE,{"disambiguationData":[TD([[subQ2,-1.0]])],"derivedFrom":subQ1}),-1.0]])]});}
            var Q9;
            {var subQ0=sQuery(id+"F0.wireOp",EDGE,"E4.right");var subQ1=sQuery(id+"F0.wireOp",EDGE,"E4.top");var subQ2=makeQuery(id+"F0.imprint","INTERSECT",VERTEX,{"derivedFrom":[subQ1,subQ0]});Q9=makeQuery(id+"F0.imprint","IMPRINT",FACE,{"disambiguationData":[TD([[makeQuery(id+"F0.imprint","IMPRINT",EDGE,{"disambiguationData":[TD([[subQ2,1.0]])],"derivedFrom":subQ1}),-1.0]])]});}
            var Q10;
            {var subQ0=sQuery(id+"F0.wireOp",EDGE,"E94");Q10=makeQuery(id+"F0.imprint","IMPRINT",FACE,{"disambiguationData":[TD([[makeQuery(id+"F0.imprint","IMPRINT",EDGE,{"derivedFrom":subQ0}),-1.0]])]});}
            var Q11;
            {var subQ2=sQuery(id+"F0.wireOp",EDGE,"E95");Q11=makeQuery(id+"F0.imprint","IMPRINT",FACE,{"disambiguationData":[TD([[makeQuery(id+"F0.imprint","IMPRINT",EDGE,{"derivedFrom":subQ2}),-1.0]])]});}
            var Q12;
            {var subQ21=sQuery(id+"F0.wireOp",EDGE,"E86");Q12=makeQuery(id+"F0.imprint","IMPRINT",FACE,{"disambiguationData":[TD([[makeQuery(id+"F0.imprint","IMPRINT",EDGE,{"derivedFrom":subQ21}),1.0]])]});}
            var Q13;
            {var subQ0=sQuery(id+"F0.wireOp",EDGE,"E7.MirrorCS");var subQ1=sQuery(id+"F0.wireOp",EDGE,"E6.MirrorCS");var subQ2=makeQuery(id+"F0.imprint","INTERSECT",VERTEX,{"derivedFrom":[subQ1,subQ0]});Q13=makeQuery(id+"F0.imprint","IMPRINT",FACE,{"disambiguationData":[TD([[makeQuery(id+"F0.imprint","IMPRINT",EDGE,{"disambiguationData":[TD([[subQ2,-1.0]])],"derivedFrom":subQ1}),-1.0]])]});}
            var Q14;
            {var subQ0=sQuery(id+"F0.wireOp",EDGE,"E6.MirrorCS");var subQ1=sQuery(id+"F0.wireOp",EDGE,"E5.MirrorCS");var subQ2=makeQuery(id+"F0.imprint","INTERSECT",VERTEX,{"derivedFrom":[subQ1,subQ0]});Q14=makeQuery(id+"F0.imprint","IMPRINT",FACE,{"disambiguationData":[TD([[makeQuery(id+"F0.imprint","IMPRINT",EDGE,{"disambiguationData":[TD([[subQ2,-1.0]])],"derivedFrom":subQ1}),-1.0]])]});}
            var Q15;
            {var subQ0=sQuery(id+"F0.wireOp",EDGE,"E8.MirrorCS");var subQ1=sQuery(id+"F0.wireOp",EDGE,"E5.MirrorCS");var subQ2=makeQuery(id+"F0.imprint","INTERSECT",VERTEX,{"derivedFrom":[subQ1,subQ0]});Q15=makeQuery(id+"F0.imprint","IMPRINT",FACE,{"disambiguationData":[TD([[makeQuery(id+"F0.imprint","IMPRINT",EDGE,{"disambiguationData":[TD([[subQ2,1.0]])],"derivedFrom":subQ1}),-1.0]])]});}
            var Q16;
            {var subQ0=sQuery(id+"F0.wireOp",EDGE,"E8.MirrorCS");var subQ1=sQuery(id+"F0.wireOp",EDGE,"E7.MirrorCS");var subQ2=makeQuery(id+"F0.imprint","INTERSECT",VERTEX,{"derivedFrom":[subQ1,subQ0]});Q16=makeQuery(id+"F0.imprint","IMPRINT",FACE,{"disambiguationData":[TD([[makeQuery(id+"F0.imprint","IMPRINT",EDGE,{"disambiguationData":[TD([[subQ2,1.0]])],"derivedFrom":subQ1}),1.0]])]});}
            var Q17;
            {var subQ0=sQuery(id+"F0.wireOp",EDGE,"E36.MirrorCS");var subQ1=sQuery(id+"F0.wireOp",EDGE,"E33.MirrorCS");var subQ2=makeQuery(id+"F0.imprint","INTERSECT",VERTEX,{"derivedFrom":[subQ1,subQ0]});Q17=makeQuery(id+"F0.imprint","IMPRINT",FACE,{"disambiguationData":[TD([[makeQuery(id+"F0.imprint","IMPRINT",EDGE,{"disambiguationData":[TD([[subQ2,-1.0]])],"derivedFrom":subQ1}),1.0]])]});}
            var Q18;
            {var subQ0=sQuery(id+"F0.wireOp",EDGE,"E36.MirrorCS");var subQ1=sQuery(id+"F0.wireOp",EDGE,"E35.MirrorCS");var subQ2=makeQuery(id+"F0.imprint","INTERSECT",VERTEX,{"derivedFrom":[subQ1,subQ0]});Q18=makeQuery(id+"F0.imprint","IMPRINT",FACE,{"disambiguationData":[TD([[makeQuery(id+"F0.imprint","IMPRINT",EDGE,{"disambiguationData":[TD([[subQ2,-1.0]])],"derivedFrom":subQ1}),-1.0]])]});}
            var Q19;
            {var subQ0=sQuery(id+"F0.wireOp",EDGE,"E37.MirrorCS");var subQ1=sQuery(id+"F0.wireOp",EDGE,"E35.MirrorCS");var subQ2=makeQuery(id+"F0.imprint","INTERSECT",VERTEX,{"derivedFrom":[subQ1,subQ0]});Q19=makeQuery(id+"F0.imprint","IMPRINT",FACE,{"disambiguationData":[TD([[makeQuery(id+"F0.imprint","IMPRINT",EDGE,{"disambiguationData":[TD([[subQ2,1.0]])],"derivedFrom":subQ1}),-1.0]])]});}
            var Q20;
            {var subQ0=sQuery(id+"F0.wireOp",EDGE,"E37.MirrorCS");var subQ1=sQuery(id+"F0.wireOp",EDGE,"E33.MirrorCS");var subQ2=makeQuery(id+"F0.imprint","INTERSECT",VERTEX,{"derivedFrom":[subQ1,subQ0]});Q20=makeQuery(id+"F0.imprint","IMPRINT",FACE,{"disambiguationData":[TD([[makeQuery(id+"F0.imprint","IMPRINT",EDGE,{"disambiguationData":[TD([[subQ2,1.0]])],"derivedFrom":subQ1}),1.0]])]});}
            extrude(context, id + "F4", {"entities" : qUnion([Q0, Q1, Q2, Q3, Q4, Q5, Q6, Q7, Q8, Q9, Q10, Q11, Q12, Q13, Q14, Q15, Q16, Q17, Q18, Q19, Q20]), "endBound" : BoundingType.SYMMETRIC, "depth" : 3.17 * mm});
        }
    });
